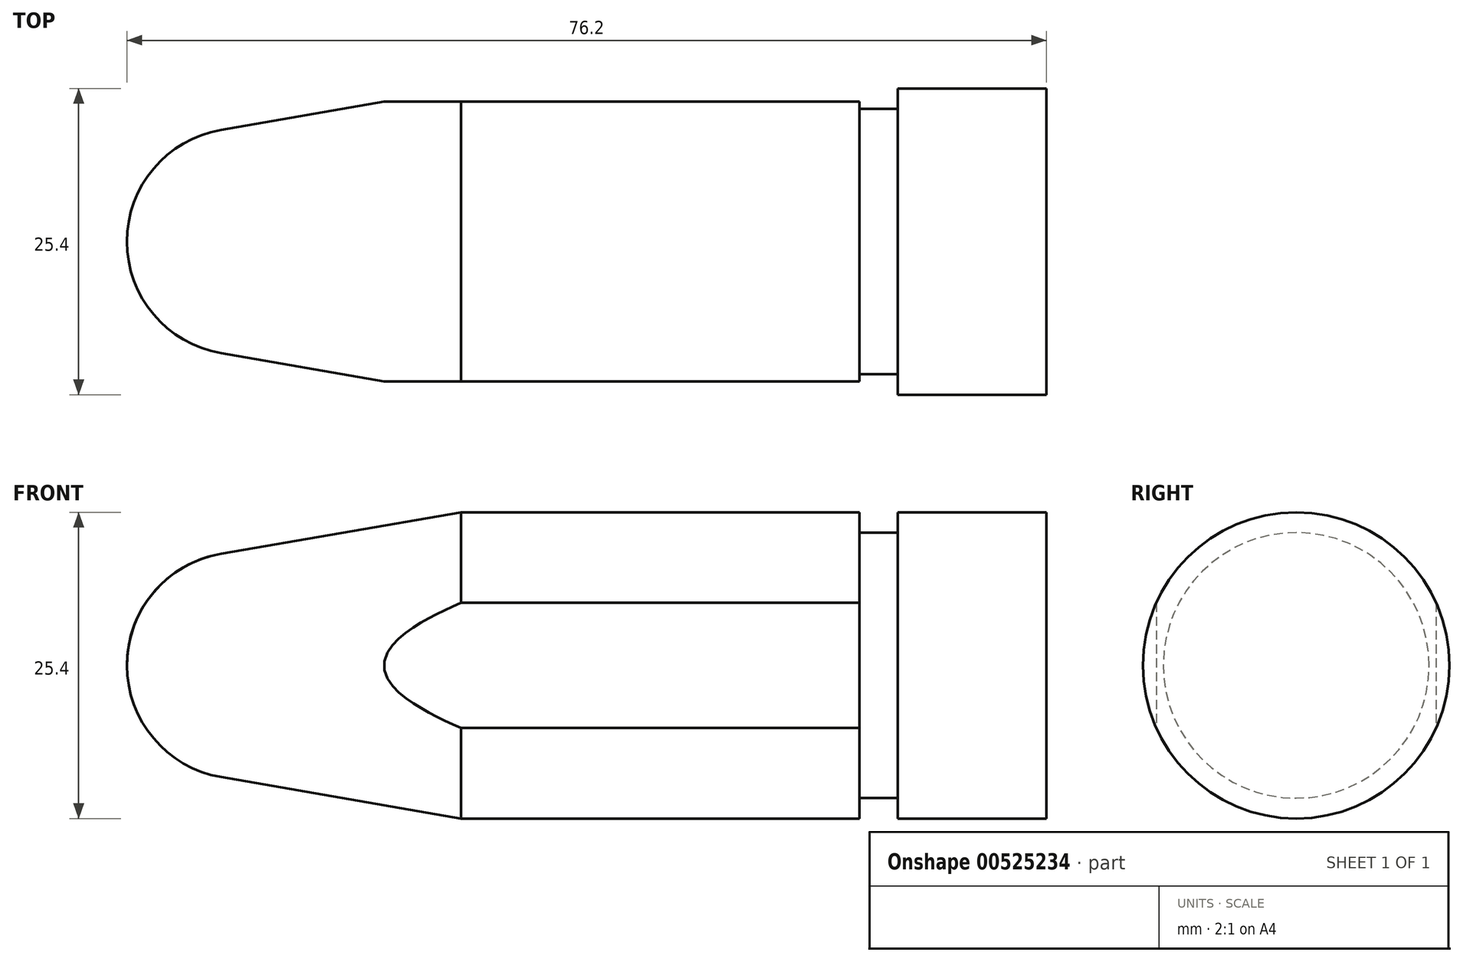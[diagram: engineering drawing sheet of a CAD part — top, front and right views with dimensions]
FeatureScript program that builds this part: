
annotation { "Feature Type Name" : "Feature", "Feature Type Description" : "" }
export const myFeature = defineFeature(function(context is Context, id is Id, definition is map)
    precondition{}
    {
        {
            var Q0;
            Q0=qCreatedBy(makeId("Right.planeOp"),FACE);
            var sketch = newSketch(context, id + "F0", { "sketchPlane" : qUnion([Q0])});
            skCircle(sketch, "E0", {"center": v(0, 0) * mm, "radius": 12.7 * mm});
            skSolve(sketch);
        }
        {
            var Q0;
            Q0=makeQuery(id+"F0.imprint","IMPRINT",FACE,{"disambiguationData":[TD([[makeQuery(id+"F0.imprint","IMPRINT",EDGE,{"derivedFrom":sQuery(id+"F0.wireOp",EDGE,"E0")}),1.0]])]});
            var Q1;
            Q1=sQuery(id+"F0.wireOp",EDGE,"E0");
            extrude(context, id + "F1", {"entities" : qUnion([Q0]), "surfaceEntities" : qUnion([Q1]), "depth" : 12.32 * mm, "offsetDistance" : 25.4 * mm});
        }
        {
            var Q0;
            Q0=makeQuery(id+"F1.opExtrude","CAP_FACE",FACE,{"disambiguationData":[OSD([sQuery(id+"F0.wireOp",EDGE,"E0")])],"isStart":true});
            var sketch = newSketch(context, id + "F2", { "sketchPlane" : qUnion([Q0])});
            skCircle(sketch, "E1", {"center": v(0, 0) * mm, "radius": 11.01 * mm});
            skSolve(sketch);
        }
        {
            var Q0;
            Q0=makeQuery(id+"F2.imprint","IMPRINT",FACE,{"disambiguationData":[TD([[makeQuery(id+"F2.imprint","IMPRINT",EDGE,{"derivedFrom":sQuery(id+"F2.wireOp",EDGE,"E1")}),1.0]])]});
            extrude(context, id + "F3", {"entities" : qUnion([Q0]), "operationType" : NewBodyOperationType.ADD, "depth" : 3.17 * mm, "offsetDistance" : 25.4 * mm});
        }
        {
            var Q0;
            Q0=makeQuery(id+"F3.opExtrude","CAP_FACE",FACE,{"disambiguationData":[OSD([sQuery(id+"F2.wireOp",EDGE,"E1")])],"isStart":false});
            var sketch = newSketch(context, id + "F4", { "sketchPlane" : qUnion([Q0])});
            skArc(sketch, "E2", {"start": v(-11.6, -5.18) * mm, "mid": v(0, -12.7) * mm, "end": v(11.6, -5.18) * mm});
            skLineSegment(sketch, "E3", {"start": v(-11.6, 5.18) * mm, "end": v(-11.6, -5.18) * mm});
            skLineSegment(sketch, "E4", {"start": v(11.6, 5.18) * mm, "end": v(11.6, -5.18) * mm});
            skArc(sketch, "E5.trimOffspring", {"start": v(11.6, 5.18) * mm, "mid": v(0, 12.7) * mm, "end": v(-11.6, 5.18) * mm});
            skSolve(sketch);
        }
        {
            var Q0;
            Q0 = qSketchRegion(id + "F4", true);
            extrude(context, id + "F5", {"entities" : qUnion([Q0]), "operationType" : NewBodyOperationType.ADD, "depth" : 33.02 * mm, "offsetDistance" : 25.4 * mm});
        }
        {
            var Q0;
            Q0=qCreatedBy(makeId("Front.planeOp"),FACE);
            var sketch = newSketch(context, id + "F6", { "sketchPlane" : qUnion([Q0])});
            skArc(sketch, "E6", {"start": v(-56.08, 9.26) * mm, "mid": v(-61.67, 6.05) * mm, "end": v(-63.88, 0) * mm});
            skLineSegment(sketch, "E7", {"start": v(-36.2, 12.7) * mm, "end": v(-56.08, 9.26) * mm});
            skLineSegment(sketch, "E8", {"start": v(-36.2, 12.7) * mm, "end": v(-36.2, 0) * mm});
            skLineSegment(sketch, "E9", {"start": v(-63.88, 0) * mm, "end": v(-36.2, 0) * mm});
            skSolve(sketch);
        }
        {
            var Q0;
            Q0=makeQuery(id+"F6.imprint","IMPRINT",FACE,{"disambiguationData":[TD([[makeQuery(id+"F6.imprint","IMPRINT",EDGE,{"derivedFrom":sQuery(id+"F6.wireOp",EDGE,"E6")}),1.0]])]});
            var Q1;
            Q1=sQuery(id+"F6.wireOp",EDGE,"E9");
            revolve(context, id + "F7", {"operationType" : NewBodyOperationType.ADD, "entities" : qUnion([Q0]), "axis" : qUnion([Q1]), "revolveType" : RevolveType.FULL});
        }
        {
            var Q0;
            Q0=makeQuery(id+"F7.boolean.opBoolean","SPLIT",FACE,{"disambiguationData":[TD([makeQuery(id+"F5.opExtrude","SWEPT_FACE",FACE,{"disambiguationData":[OSD([sQuery(id+"F4.wireOp",EDGE,"E4")])]})])],"derivedFrom":makeQuery(id+"F7.opRevolve","SWEPT_FACE",FACE,{"disambiguationData":[OSD([sQuery(id+"F6.wireOp",EDGE,"E8")])]})});
            var sketch = newSketch(context, id + "F8", { "sketchPlane" : qUnion([Q0])});
            skCircle(sketch, "E10", {"center": v(0, 0) * mm, "radius": 12.7 * mm});
            skLineSegment(sketch, "E11", {"start": v(-11.6, 5.18) * mm, "end": v(-11.6, -5.18) * mm});
            skArc(sketch, "E12", {"start": v(-11.6, 5.18) * mm, "mid": v(-12.97, 0) * mm, "end": v(-11.6, -5.18) * mm});
            skLineSegment(sketch, "E13.MirrorCS", {"start": v(11.6, 5.18) * mm, "end": v(11.6, -5.18) * mm});
            skArc(sketch, "E14.MirrorCS", {"start": v(11.6, 5.18) * mm, "mid": v(12.97, 0) * mm, "end": v(11.6, -5.18) * mm});
            skSolve(sketch);
        }
        {
            var Q0;
            {var subQ1=sQuery(id+"F8.wireOp",EDGE,"E11");Q0=makeQuery(id+"F8.imprint","IMPRINT",FACE,{"disambiguationData":[TD([[makeQuery(id+"F8.imprint","IMPRINT",EDGE,{"derivedFrom":subQ1}),-1.0]])]});}
            extrude(context, id + "F9", {"entities" : qUnion([Q0]), "operationType" : NewBodyOperationType.REMOVE, "oppositeDirection" : true, "depth" : 25.4 * mm, "offsetDistance" : 25.4 * mm});
        }
        {
            var Q0;
            Q0=makeQuery(id+"F7.boolean.opBoolean","SPLIT",FACE,{"disambiguationData":[TD([makeQuery(id+"F5.opExtrude","SWEPT_FACE",FACE,{"disambiguationData":[OSD([sQuery(id+"F4.wireOp",EDGE,"E3")])]})])],"derivedFrom":makeQuery(id+"F7.opRevolve","SWEPT_FACE",FACE,{"disambiguationData":[OSD([sQuery(id+"F6.wireOp",EDGE,"E8")])]})});
            extrude(context, id + "F10", {"entities" : qUnion([Q0]), "operationType" : NewBodyOperationType.REMOVE, "oppositeDirection" : true, "depth" : 25.4 * mm, "offsetDistance" : 25.4 * mm});
        }
    });
